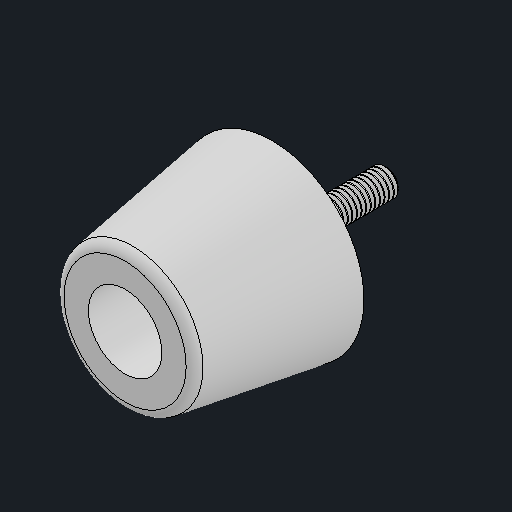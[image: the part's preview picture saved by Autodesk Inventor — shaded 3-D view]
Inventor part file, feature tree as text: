
AUTODESK INVENTOR PART (.ipt)
format: ipt  version: 2024.2 (Build 282272000, 272)  size: 253,952 bytes
history: native  units: mm
features: other x5, fillet x1
ambient origin geometry x8: Origin, YZ Plane, XZ Plane, XY Plane, X Axis, Y Axis, Z Axis, Center Point
bodies: Body1 (feature_tree), Body2 (feature_tree), Body3 (feature_tree)
feature tree (6):
  other  "솔리드1"
  other  "솔리드2"
  other  "솔리드3"
  fillet  "Fillet1"  [1 undecoded]
  other  "Boss-Extrude1"
  other  "_shcs-M3-ndr_-_ThdSchPat_"
note: 1 required parameter value undecoded (feature->parameter linkage not recoverable at this tier; creation-order binding heuristic only, values carry confidence <= 0.55)
